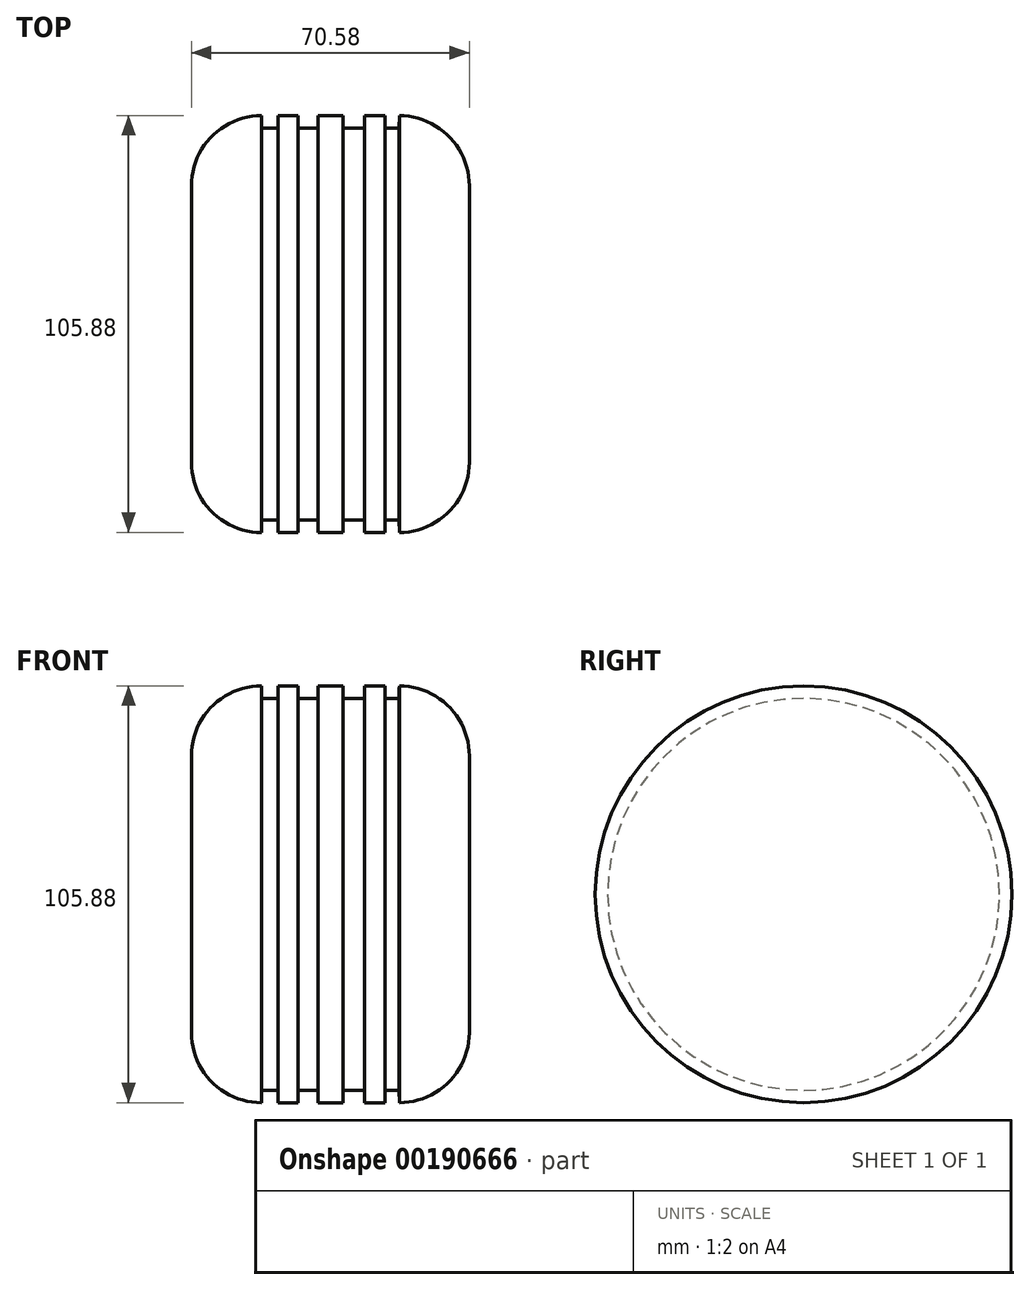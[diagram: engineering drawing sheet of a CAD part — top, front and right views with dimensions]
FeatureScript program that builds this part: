
annotation { "Feature Type Name" : "Feature", "Feature Type Description" : "" }
export const myFeature = defineFeature(function(context is Context, id is Id, definition is map)
    precondition{}
    {
        {
            var Q0;
            Q0=qCreatedBy(makeId("Front.planeOp"),FACE);
            var sketch = newSketch(context, id + "F0", { "sketchPlane" : qUnion([Q0])});
            skLineSegment(sketch, "E0.bottom", {"start": v(13.83, 52.94) * mm, "end": v(8.65, 52.94) * mm});
            skLineSegment(sketch, "E0.left", {"start": v(35.3, 35.16) * mm, "end": v(35.3, 0) * mm});
            skLineSegment(sketch, "E0.right", {"start": v(-35.3, 35.16) * mm, "end": v(-35.3, 0) * mm});
            skPoint(sketch, "E0.middle", {"position": v(0, 0) * mm});
            skPoint(sketch, "E1.visualSharp", {"position": v(-35.3, 52.94) * mm});
            skArc(sketch, "E1.filletArc", {"start": v(-17.51, 52.94) * mm, "mid": v(-30.09, 47.73) * mm, "end": v(-35.3, 35.16) * mm});
            skPoint(sketch, "E2.visualSharp", {"position": v(35.3, 52.94) * mm});
            skArc(sketch, "E2.filletArc", {"start": v(35.3, 35.16) * mm, "mid": v(30.09, 47.73) * mm, "end": v(17.51, 52.94) * mm});
            skPoint(sketch, "E3.visualSharp", {"position": v(-35.3, -52.94) * mm});
            skPoint(sketch, "E4.visualSharp", {"position": v(35.3, -52.94) * mm});
            skLineSegment(sketch, "E5", {"start": v(-17.51, 52.94) * mm, "end": v(-17.51, 49.78) * mm});
            skLineSegment(sketch, "E6", {"start": v(-17.51, 49.78) * mm, "end": v(-13.32, 49.78) * mm});
            skLineSegment(sketch, "E7", {"start": v(17.45, 49.78) * mm, "end": v(17.51, 52.94) * mm});
            skLineSegment(sketch, "E8", {"start": v(-0.03, 52.94) * mm, "end": v(0.02, 49.78) * mm});
            skPoint(sketch, "E8.startSnap0", {"position": v(-0.03, 49.78) * mm});
            skLineSegment(sketch, "E9", {"start": v(13.83, 49.78) * mm, "end": v(13.83, 52.94) * mm});
            skLineSegment(sketch, "E10", {"start": v(-35.3, 0) * mm, "end": v(35.3, 0) * mm});
            skPoint(sketch, "E3.filletArc.start.orphan", {"position": v(-35.3, -35.16) * mm});
            skPoint(sketch, "E11.orphan", {"position": v(35.3, -35.16) * mm});
            skLineSegment(sketch, "E12", {"start": v(-13.32, 52.94) * mm, "end": v(-13.32, 49.78) * mm});
            skLineSegment(sketch, "E13", {"start": v(-8.15, 52.94) * mm, "end": v(-8.15, 49.78) * mm});
            skLineSegment(sketch, "E14", {"start": v(-3.11, 52.94) * mm, "end": v(-3.11, 49.78) * mm});
            skLineSegment(sketch, "E15", {"start": v(8.65, 52.94) * mm, "end": v(8.65, 49.78) * mm});
            skLineSegment(sketch, "E16", {"start": v(3.22, 52.94) * mm, "end": v(3.22, 49.78) * mm});
            skLineSegment(sketch, "E17.trimOffspring", {"start": v(-8.15, 52.94) * mm, "end": v(-13.32, 52.94) * mm});
            skLineSegment(sketch, "E18.trimOffspring", {"start": v(-8.15, 49.78) * mm, "end": v(-3.11, 49.78) * mm});
            skLineSegment(sketch, "E19.trimOffspring", {"start": v(3.22, 52.94) * mm, "end": v(-3.11, 52.94) * mm});
            skLineSegment(sketch, "E20.trimOffspring", {"start": v(3.22, 49.78) * mm, "end": v(8.65, 49.78) * mm});
            skLineSegment(sketch, "E21.trimOffspring", {"start": v(-0.03, 49.78) * mm, "end": v(0.02, 49.78) * mm});
            skLineSegment(sketch, "E22.trimOffspring", {"start": v(13.83, 49.78) * mm, "end": v(17.45, 49.78) * mm});
            skSolve(sketch);
        }
        {
            var Q0;
            Q0=makeQuery(id+"F0.imprint","IMPRINT",FACE,{"disambiguationData":[TD([[makeQuery(id+"F0.imprint","IMPRINT",EDGE,{"derivedFrom":sQuery(id+"F0.wireOp",EDGE,"E0.bottom")}),1.0]])]});
            var Q1;
            Q1=sQuery(id+"F0.wireOp",EDGE,"E10");
            revolve(context, id + "F1", {"entities" : qUnion([Q0]), "axis" : qUnion([Q1]), "revolveType" : RevolveType.FULL});
        }
    });
